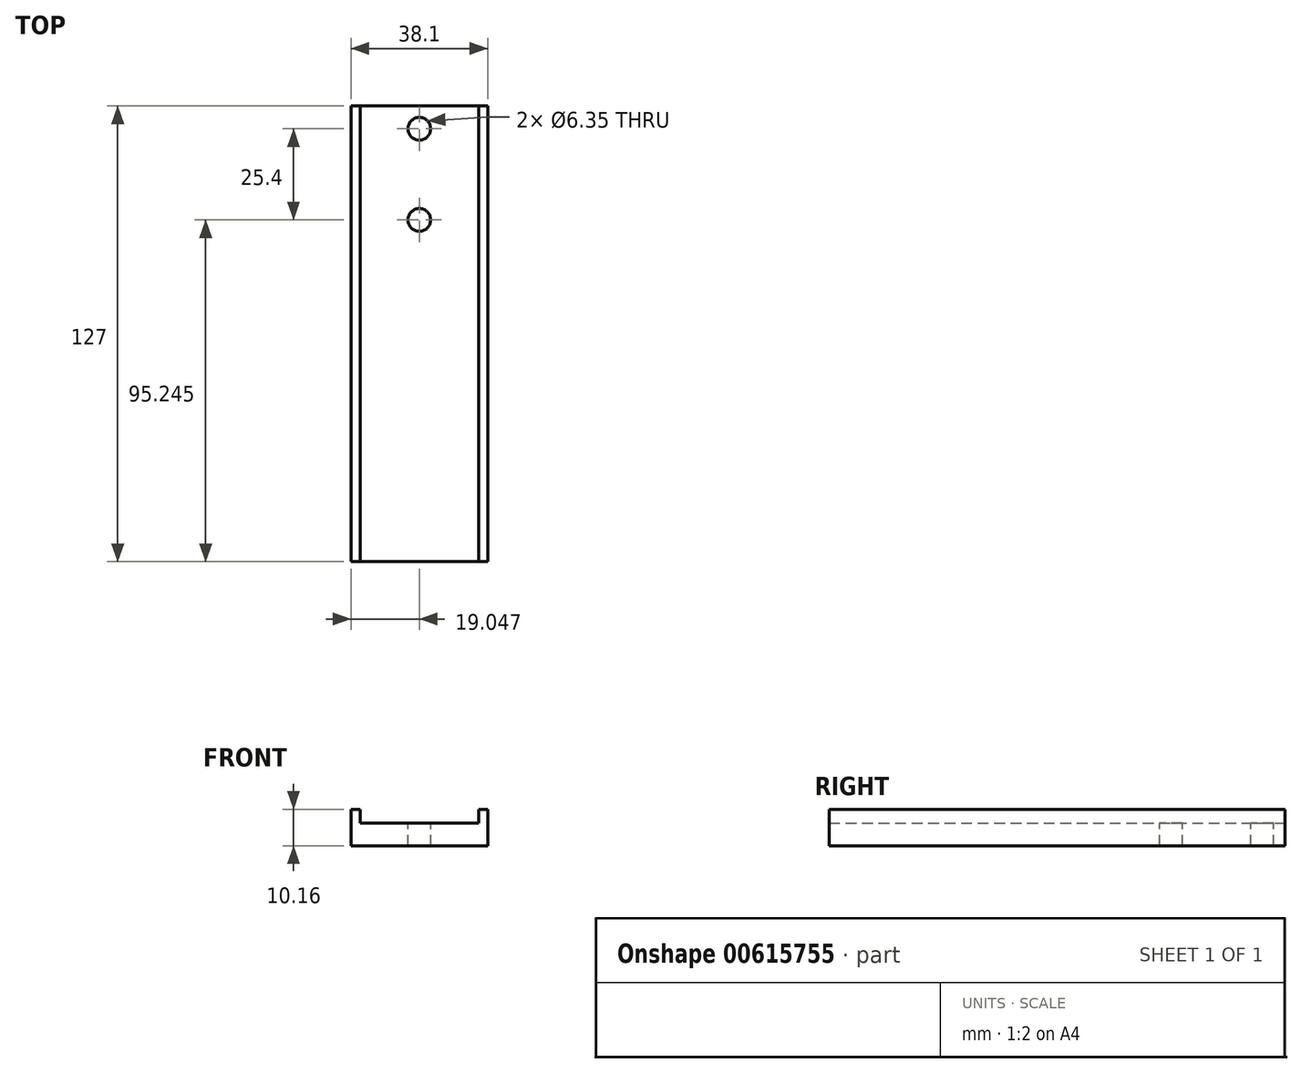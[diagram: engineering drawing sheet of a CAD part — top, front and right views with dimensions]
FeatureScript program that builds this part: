
annotation { "Feature Type Name" : "Feature", "Feature Type Description" : "" }
export const myFeature = defineFeature(function(context is Context, id is Id, definition is map)
    precondition{}
    {
        {
            var Q0;
            Q0=qCreatedBy(makeId("Top.planeOp"),FACE);
            var sketch = newSketch(context, id + "F0", { "sketchPlane" : qUnion([Q0])});
            skLineSegment(sketch, "E0.bottom", {"start": v(-21, 85.79) * mm, "end": v(17.1, 85.79) * mm});
            skLineSegment(sketch, "E0.top", {"start": v(-21, -41.21) * mm, "end": v(17.1, -41.21) * mm});
            skLineSegment(sketch, "E0.left", {"start": v(-21, 85.79) * mm, "end": v(-21, -41.21) * mm});
            skLineSegment(sketch, "E0.right", {"start": v(17.1, 85.79) * mm, "end": v(17.1, -41.21) * mm});
            skSolve(sketch);
        }
        {
            var Q0;
            Q0 = qSketchRegion(id + "F0", true);
            extrude(context, id + "F1", {"entities" : qUnion([Q0]), "depth" : 6.35 * mm, "offsetDistance" : 25.4 * mm});
        }
        {
            var Q0;
            Q0=makeQuery(id+"F1.opExtrude","CAP_FACE",FACE,{"disambiguationData":[OSD([sQuery(id+"F0.wireOp",EDGE,"E0.bottom"),sQuery(id+"F0.wireOp",EDGE,"E0.top"),sQuery(id+"F0.wireOp",EDGE,"E0.left"),sQuery(id+"F0.wireOp",EDGE,"E0.right")])],"isStart":false});
            var sketch = newSketch(context, id + "F2", { "sketchPlane" : qUnion([Q0])});
            skLineSegment(sketch, "E1.bottom", {"start": v(-21, 85.79) * mm, "end": v(-18.45, 85.79) * mm});
            skLineSegment(sketch, "E1.top", {"start": v(-21, -41.21) * mm, "end": v(-18.45, -41.21) * mm});
            skLineSegment(sketch, "E1.left", {"start": v(-21, 85.79) * mm, "end": v(-21, -41.21) * mm});
            skLineSegment(sketch, "E1.right", {"start": v(-18.45, 85.79) * mm, "end": v(-18.45, -41.21) * mm});
            skLineSegment(sketch, "E2.bottom", {"start": v(17.1, -41.21) * mm, "end": v(14.57, -41.21) * mm});
            skLineSegment(sketch, "E2.top", {"start": v(17.1, 85.79) * mm, "end": v(14.57, 85.79) * mm});
            skLineSegment(sketch, "E2.left", {"start": v(17.1, -41.21) * mm, "end": v(17.1, 85.79) * mm});
            skLineSegment(sketch, "E2.right", {"start": v(14.57, -41.21) * mm, "end": v(14.57, 85.79) * mm});
            skSolve(sketch);
        }
        {
            var Q0;
            Q0 = qSketchRegion(id + "F2", true);
            extrude(context, id + "F3", {"entities" : qUnion([Q0]), "operationType" : NewBodyOperationType.ADD, "depth" : 3.8 * mm, "offsetDistance" : 25.4 * mm});
        }
        {
            var Q0;
            Q0=makeQuery(id+"F1.opExtrude","CAP_FACE",FACE,{"disambiguationData":[OSD([sQuery(id+"F0.wireOp",EDGE,"E0.bottom"),sQuery(id+"F0.wireOp",EDGE,"E0.top"),sQuery(id+"F0.wireOp",EDGE,"E0.left"),sQuery(id+"F0.wireOp",EDGE,"E0.right")])],"isStart":false});
            var sketch = newSketch(context, id + "F4", { "sketchPlane" : qUnion([Q0])});
            skCircle(sketch, "E3", {"center": v(-1.94, 79.44) * mm, "radius": 3.18 * mm});
            skCircle(sketch, "E4", {"center": v(-1.94, 54.04) * mm, "radius": 3.18 * mm});
            skSolve(sketch);
        }
        {
            var Q0;
            Q0 = qSketchRegion(id + "F4", true);
            extrude(context, id + "F5", {"entities" : qUnion([Q0]), "operationType" : NewBodyOperationType.REMOVE, "oppositeDirection" : true, "depth" : 6.35 * mm, "offsetDistance" : 25.4 * mm});
        }
    });
